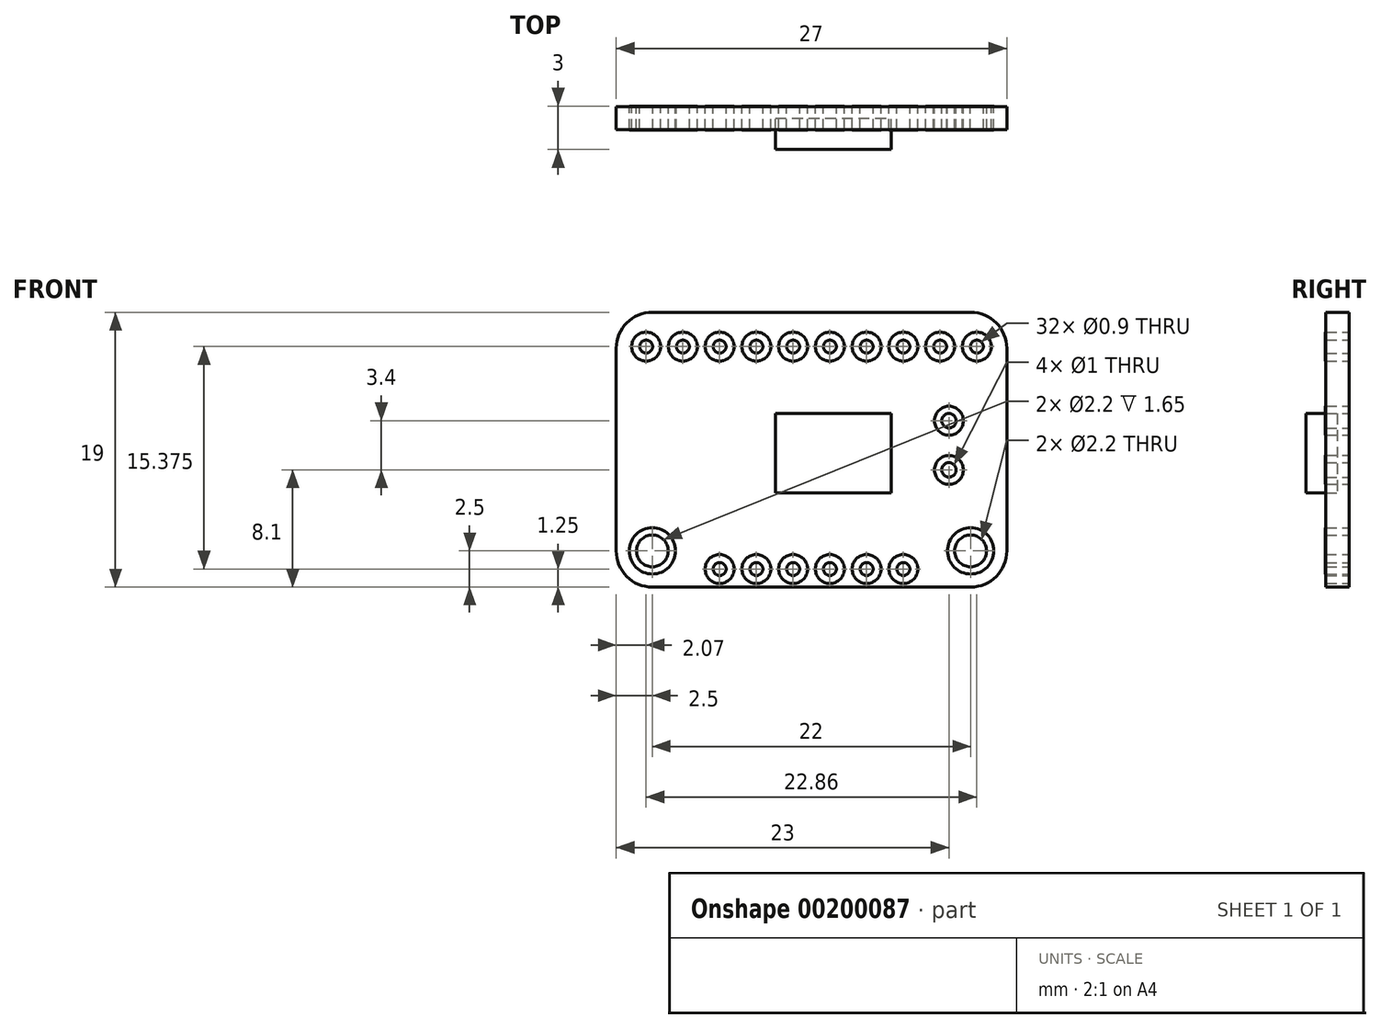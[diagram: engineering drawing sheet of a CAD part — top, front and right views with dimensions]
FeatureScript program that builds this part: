
annotation { "Feature Type Name" : "Feature", "Feature Type Description" : "" }
export const myFeature = defineFeature(function(context is Context, id is Id, definition is map)
    precondition{}
    {
        {
            var Q0;
            Q0=qCreatedBy(makeId("Front.planeOp"),FACE);
            var sketch = newSketch(context, id + "F0", { "sketchPlane" : qUnion([Q0])});
            skLineSegment(sketch, "E0.bottom", {"start": v(11, 9.5) * mm, "end": v(-11, 9.5) * mm});
            skLineSegment(sketch, "E0.top", {"start": v(11, -9.5) * mm, "end": v(-11, -9.5) * mm});
            skLineSegment(sketch, "E0.left", {"start": v(13.5, 7) * mm, "end": v(13.5, -7) * mm});
            skLineSegment(sketch, "E0.right", {"start": v(-13.5, 7) * mm, "end": v(-13.5, -7) * mm});
            skPoint(sketch, "E0.middle", {"position": v(0, 0) * mm});
            skPoint(sketch, "E1.visualSharp", {"position": v(-13.5, 9.5) * mm});
            skArc(sketch, "E1.filletArc", {"start": v(-11, 9.5) * mm, "mid": v(-12.77, 8.77) * mm, "end": v(-13.5, 7) * mm});
            skPoint(sketch, "E2.visualSharp", {"position": v(13.5, 9.5) * mm});
            skArc(sketch, "E2.filletArc", {"start": v(13.5, 7) * mm, "mid": v(12.77, 8.77) * mm, "end": v(11, 9.5) * mm});
            skPoint(sketch, "E3.visualSharp", {"position": v(13.5, -9.5) * mm});
            skArc(sketch, "E3.filletArc", {"start": v(11, -9.5) * mm, "mid": v(12.77, -8.77) * mm, "end": v(13.5, -7) * mm});
            skPoint(sketch, "E4.visualSharp", {"position": v(-13.5, -9.5) * mm});
            skArc(sketch, "E4.filletArc", {"start": v(-13.5, -7) * mm, "mid": v(-12.77, -8.77) * mm, "end": v(-11, -9.5) * mm});
            skCircle(sketch, "E5", {"center": v(-11, -7) * mm, "radius": 1.1 * mm});
            skCircle(sketch, "E6", {"center": v(11, -7) * mm, "radius": 1.1 * mm});
            skLineSegment(sketch, "E7.bottom", {"start": v(-2.5, 2.5) * mm, "end": v(5.5, 2.5) * mm});
            skLineSegment(sketch, "E7.top", {"start": v(-2.5, -3) * mm, "end": v(5.5, -3) * mm});
            skLineSegment(sketch, "E7.left", {"start": v(-2.5, 2.5) * mm, "end": v(-2.5, -3) * mm});
            skLineSegment(sketch, "E7.right", {"start": v(5.5, 2.5) * mm, "end": v(5.5, -3) * mm});
            skPoint(sketch, "E7.middle", {"position": v(1.5, -0.25) * mm});
            skCircle(sketch, "E8", {"center": v(9.5, 2) * mm, "radius": 0.5 * mm});
            skCircle(sketch, "E9", {"center": v(9.5, -1.4) * mm, "radius": 0.5 * mm});
            skCircle(sketch, "E10", {"center": v(-11.43, 7.13) * mm, "radius": 0.45 * mm});
            skCircle(sketch, "E11.1.0.0", {"center": v(-8.9, 7.13) * mm, "radius": 0.45 * mm});
            skCircle(sketch, "E11.2.0.0", {"center": v(-6.35, 7.13) * mm, "radius": 0.45 * mm});
            skCircle(sketch, "E11.3.0.0", {"center": v(-3.81, 7.13) * mm, "radius": 0.45 * mm});
            skCircle(sketch, "E11.4.0.0", {"center": v(-1.27, 7.13) * mm, "radius": 0.45 * mm});
            skCircle(sketch, "E11.5.0.0", {"center": v(1.27, 7.13) * mm, "radius": 0.45 * mm});
            skCircle(sketch, "E11.6.0.0", {"center": v(3.8, 7.13) * mm, "radius": 0.45 * mm});
            skCircle(sketch, "E11.7.0.0", {"center": v(6.35, 7.13) * mm, "radius": 0.45 * mm});
            skCircle(sketch, "E11.8.0.0", {"center": v(8.89, 7.13) * mm, "radius": 0.45 * mm});
            skCircle(sketch, "E11.9.0.0", {"center": v(11.43, 7.13) * mm, "radius": 0.45 * mm});
            skLineSegment(sketch, "E11.direction1", {"start": v(-11.43, 7.13) * mm, "end": v(-8.89, 7.13) * mm, "construction": true});
            skCircle(sketch, "E12", {"center": v(-6.35, -8.25) * mm, "radius": 0.45 * mm});
            skCircle(sketch, "E13.1.0.0", {"center": v(-3.81, -8.25) * mm, "radius": 0.45 * mm});
            skCircle(sketch, "E13.2.0.0", {"center": v(-1.27, -8.25) * mm, "radius": 0.45 * mm});
            skCircle(sketch, "E13.3.0.0", {"center": v(1.27, -8.25) * mm, "radius": 0.45 * mm});
            skCircle(sketch, "E13.4.0.0", {"center": v(3.81, -8.25) * mm, "radius": 0.45 * mm});
            skCircle(sketch, "E13.5.0.0", {"center": v(6.35, -8.25) * mm, "radius": 0.45 * mm});
            skLineSegment(sketch, "E13.direction1", {"start": v(-6.35, -8.25) * mm, "end": v(-3.81, -8.25) * mm, "construction": true});
            skCircle(sketch, "E14", {"center": v(9.5, -1.4) * mm, "radius": 1 * mm});
            skCircle(sketch, "E15", {"center": v(9.5, 2) * mm, "radius": 1 * mm});
            skCircle(sketch, "E16", {"center": v(-6.35, -8.25) * mm, "radius": 1 * mm});
            skCircle(sketch, "E17.1.0.0", {"center": v(-3.81, -8.25) * mm, "radius": 1 * mm});
            skCircle(sketch, "E17.2.0.0", {"center": v(-1.27, -8.25) * mm, "radius": 1 * mm});
            skCircle(sketch, "E17.3.0.0", {"center": v(1.27, -8.25) * mm, "radius": 1 * mm});
            skCircle(sketch, "E17.4.0.0", {"center": v(3.8, -8.25) * mm, "radius": 1 * mm});
            skCircle(sketch, "E17.5.0.0", {"center": v(6.35, -8.25) * mm, "radius": 1 * mm});
            skCircle(sketch, "E18", {"center": v(-11.43, 7.13) * mm, "radius": 1 * mm});
            skCircle(sketch, "E19.1.0.0", {"center": v(-8.9, 7.13) * mm, "radius": 1 * mm});
            skCircle(sketch, "E19.2.0.0", {"center": v(-6.35, 7.13) * mm, "radius": 1 * mm});
            skCircle(sketch, "E19.3.0.0", {"center": v(-3.81, 7.13) * mm, "radius": 1 * mm});
            skCircle(sketch, "E19.4.0.0", {"center": v(-1.27, 7.13) * mm, "radius": 1 * mm});
            skCircle(sketch, "E19.5.0.0", {"center": v(1.27, 7.13) * mm, "radius": 1 * mm});
            skCircle(sketch, "E19.6.0.0", {"center": v(3.8, 7.13) * mm, "radius": 1 * mm});
            skCircle(sketch, "E19.7.0.0", {"center": v(6.35, 7.13) * mm, "radius": 1 * mm});
            skCircle(sketch, "E19.8.0.0", {"center": v(8.89, 7.13) * mm, "radius": 1 * mm});
            skCircle(sketch, "E19.9.0.0", {"center": v(11.43, 7.13) * mm, "radius": 1 * mm});
            skLineSegment(sketch, "E19.direction1", {"start": v(-11.43, 7.13) * mm, "end": v(-8.9, 7.13) * mm, "construction": true});
            skCircle(sketch, "E20", {"center": v(-11, -7) * mm, "radius": 1.6 * mm});
            skCircle(sketch, "E21", {"center": v(11, -7) * mm, "radius": 1.6 * mm});
            skSolve(sketch);
        }
        {
            var Q0;
            Q0=makeQuery(id+"F0.imprint","IMPRINT",FACE,{"disambiguationData":[TD([[makeQuery(id+"F0.imprint","IMPRINT",EDGE,{"derivedFrom":sQuery(id+"F0.wireOp",EDGE,"E0.bottom")}),1.0]])]});
            var Q1;
            Q1=makeQuery(id+"F0.imprint","IMPRINT",FACE,{"disambiguationData":[TD([[makeQuery(id+"F0.imprint","IMPRINT",EDGE,{"derivedFrom":sQuery(id+"F0.wireOp",EDGE,"E7.bottom")}),-1.0]])]});
            var Q2;
            Q2=makeQuery(id+"F0.imprint","IMPRINT",FACE,{"disambiguationData":[TD([[makeQuery(id+"F0.imprint","IMPRINT",EDGE,{"derivedFrom":sQuery(id+"F0.wireOp",EDGE,"E10")}),-1.0]])]});
            var Q3;
            Q3=makeQuery(id+"F0.imprint","IMPRINT",FACE,{"disambiguationData":[TD([[makeQuery(id+"F0.imprint","IMPRINT",EDGE,{"derivedFrom":sQuery(id+"F0.wireOp",EDGE,"E11.1.0.0")}),-1.0]])]});
            var Q4;
            Q4=makeQuery(id+"F0.imprint","IMPRINT",FACE,{"disambiguationData":[TD([[makeQuery(id+"F0.imprint","IMPRINT",EDGE,{"derivedFrom":sQuery(id+"F0.wireOp",EDGE,"E11.2.0.0")}),-1.0]])]});
            var Q5;
            Q5=makeQuery(id+"F0.imprint","IMPRINT",FACE,{"disambiguationData":[TD([[makeQuery(id+"F0.imprint","IMPRINT",EDGE,{"derivedFrom":sQuery(id+"F0.wireOp",EDGE,"E11.3.0.0")}),-1.0]])]});
            var Q6;
            Q6=makeQuery(id+"F0.imprint","IMPRINT",FACE,{"disambiguationData":[TD([[makeQuery(id+"F0.imprint","IMPRINT",EDGE,{"derivedFrom":sQuery(id+"F0.wireOp",EDGE,"E11.4.0.0")}),-1.0]])]});
            var Q7;
            Q7=makeQuery(id+"F0.imprint","IMPRINT",FACE,{"disambiguationData":[TD([[makeQuery(id+"F0.imprint","IMPRINT",EDGE,{"derivedFrom":sQuery(id+"F0.wireOp",EDGE,"E11.5.0.0")}),-1.0]])]});
            var Q8;
            Q8=makeQuery(id+"F0.imprint","IMPRINT",FACE,{"disambiguationData":[TD([[makeQuery(id+"F0.imprint","IMPRINT",EDGE,{"derivedFrom":sQuery(id+"F0.wireOp",EDGE,"E11.6.0.0")}),-1.0]])]});
            var Q9;
            Q9=makeQuery(id+"F0.imprint","IMPRINT",FACE,{"disambiguationData":[TD([[makeQuery(id+"F0.imprint","IMPRINT",EDGE,{"derivedFrom":sQuery(id+"F0.wireOp",EDGE,"E11.7.0.0")}),-1.0]])]});
            var Q10;
            Q10=makeQuery(id+"F0.imprint","IMPRINT",FACE,{"disambiguationData":[TD([[makeQuery(id+"F0.imprint","IMPRINT",EDGE,{"derivedFrom":sQuery(id+"F0.wireOp",EDGE,"E11.8.0.0")}),-1.0]])]});
            var Q11;
            Q11=makeQuery(id+"F0.imprint","IMPRINT",FACE,{"disambiguationData":[TD([[makeQuery(id+"F0.imprint","IMPRINT",EDGE,{"derivedFrom":sQuery(id+"F0.wireOp",EDGE,"E11.9.0.0")}),-1.0]])]});
            var Q12;
            Q12=makeQuery(id+"F0.imprint","IMPRINT",FACE,{"disambiguationData":[TD([[makeQuery(id+"F0.imprint","IMPRINT",EDGE,{"derivedFrom":sQuery(id+"F0.wireOp",EDGE,"E8")}),-1.0]])]});
            var Q13;
            Q13=makeQuery(id+"F0.imprint","IMPRINT",FACE,{"disambiguationData":[TD([[makeQuery(id+"F0.imprint","IMPRINT",EDGE,{"derivedFrom":sQuery(id+"F0.wireOp",EDGE,"E9")}),-1.0]])]});
            var Q14;
            Q14=makeQuery(id+"F0.imprint","IMPRINT",FACE,{"disambiguationData":[TD([[makeQuery(id+"F0.imprint","IMPRINT",EDGE,{"derivedFrom":sQuery(id+"F0.wireOp",EDGE,"E13.5.0.0")}),-1.0]])]});
            var Q15;
            Q15=makeQuery(id+"F0.imprint","IMPRINT",FACE,{"disambiguationData":[TD([[makeQuery(id+"F0.imprint","IMPRINT",EDGE,{"derivedFrom":sQuery(id+"F0.wireOp",EDGE,"E13.4.0.0")}),-1.0]])]});
            var Q16;
            Q16=makeQuery(id+"F0.imprint","IMPRINT",FACE,{"disambiguationData":[TD([[makeQuery(id+"F0.imprint","IMPRINT",EDGE,{"derivedFrom":sQuery(id+"F0.wireOp",EDGE,"E13.3.0.0")}),-1.0]])]});
            var Q17;
            Q17=makeQuery(id+"F0.imprint","IMPRINT",FACE,{"disambiguationData":[TD([[makeQuery(id+"F0.imprint","IMPRINT",EDGE,{"derivedFrom":sQuery(id+"F0.wireOp",EDGE,"E13.2.0.0")}),-1.0]])]});
            var Q18;
            Q18=makeQuery(id+"F0.imprint","IMPRINT",FACE,{"disambiguationData":[TD([[makeQuery(id+"F0.imprint","IMPRINT",EDGE,{"derivedFrom":sQuery(id+"F0.wireOp",EDGE,"E13.1.0.0")}),-1.0]])]});
            var Q19;
            Q19=makeQuery(id+"F0.imprint","IMPRINT",FACE,{"disambiguationData":[TD([[makeQuery(id+"F0.imprint","IMPRINT",EDGE,{"derivedFrom":sQuery(id+"F0.wireOp",EDGE,"E12")}),-1.0]])]});
            var Q20;
            Q20=makeQuery(id+"F0.imprint","IMPRINT",FACE,{"disambiguationData":[TD([[makeQuery(id+"F0.imprint","IMPRINT",EDGE,{"derivedFrom":sQuery(id+"F0.wireOp",EDGE,"E6")}),-1.0]])]});
            var Q21;
            Q21=makeQuery(id+"F0.imprint","IMPRINT",FACE,{"disambiguationData":[TD([[makeQuery(id+"F0.imprint","IMPRINT",EDGE,{"derivedFrom":sQuery(id+"F0.wireOp",EDGE,"E5")}),-1.0]])]});
            extrude(context, id + "F1", {"entities" : qUnion([Q0, Q1, Q2, Q3, Q4, Q5, Q6, Q7, Q8, Q9, Q10, Q11, Q12, Q13, Q14, Q15, Q16, Q17, Q18, Q19, Q20, Q21]), "endBound" : BoundingType.SYMMETRIC, "depth" : 1.6 * mm});
        }
        {
            var Q0;
            Q0=makeQuery(id+"F0.imprint","IMPRINT",FACE,{"disambiguationData":[TD([[makeQuery(id+"F0.imprint","IMPRINT",EDGE,{"derivedFrom":sQuery(id+"F0.wireOp",EDGE,"E5")}),-1.0]])]});
            var Q1;
            Q1=makeQuery(id+"F0.imprint","IMPRINT",FACE,{"disambiguationData":[TD([[makeQuery(id+"F0.imprint","IMPRINT",EDGE,{"derivedFrom":sQuery(id+"F0.wireOp",EDGE,"E12")}),-1.0]])]});
            var Q2;
            Q2=makeQuery(id+"F0.imprint","IMPRINT",FACE,{"disambiguationData":[TD([[makeQuery(id+"F0.imprint","IMPRINT",EDGE,{"derivedFrom":sQuery(id+"F0.wireOp",EDGE,"E13.2.0.0")}),-1.0]])]});
            var Q3;
            Q3=makeQuery(id+"F0.imprint","IMPRINT",FACE,{"disambiguationData":[TD([[makeQuery(id+"F0.imprint","IMPRINT",EDGE,{"derivedFrom":sQuery(id+"F0.wireOp",EDGE,"E13.1.0.0")}),-1.0]])]});
            var Q4;
            Q4=makeQuery(id+"F0.imprint","IMPRINT",FACE,{"disambiguationData":[TD([[makeQuery(id+"F0.imprint","IMPRINT",EDGE,{"derivedFrom":sQuery(id+"F0.wireOp",EDGE,"E13.3.0.0")}),-1.0]])]});
            var Q5;
            Q5=makeQuery(id+"F0.imprint","IMPRINT",FACE,{"disambiguationData":[TD([[makeQuery(id+"F0.imprint","IMPRINT",EDGE,{"derivedFrom":sQuery(id+"F0.wireOp",EDGE,"E13.4.0.0")}),-1.0]])]});
            var Q6;
            Q6=makeQuery(id+"F0.imprint","IMPRINT",FACE,{"disambiguationData":[TD([[makeQuery(id+"F0.imprint","IMPRINT",EDGE,{"derivedFrom":sQuery(id+"F0.wireOp",EDGE,"E13.5.0.0")}),-1.0]])]});
            var Q7;
            Q7=makeQuery(id+"F0.imprint","IMPRINT",FACE,{"disambiguationData":[TD([[makeQuery(id+"F0.imprint","IMPRINT",EDGE,{"derivedFrom":sQuery(id+"F0.wireOp",EDGE,"E6")}),-1.0]])]});
            var Q8;
            Q8=makeQuery(id+"F0.imprint","IMPRINT",FACE,{"disambiguationData":[TD([[makeQuery(id+"F0.imprint","IMPRINT",EDGE,{"derivedFrom":sQuery(id+"F0.wireOp",EDGE,"E9")}),-1.0]])]});
            var Q9;
            Q9=makeQuery(id+"F0.imprint","IMPRINT",FACE,{"disambiguationData":[TD([[makeQuery(id+"F0.imprint","IMPRINT",EDGE,{"derivedFrom":sQuery(id+"F0.wireOp",EDGE,"E8")}),-1.0]])]});
            var Q10;
            Q10=makeQuery(id+"F0.imprint","IMPRINT",FACE,{"disambiguationData":[TD([[makeQuery(id+"F0.imprint","IMPRINT",EDGE,{"derivedFrom":sQuery(id+"F0.wireOp",EDGE,"E11.9.0.0")}),-1.0]])]});
            var Q11;
            Q11=makeQuery(id+"F0.imprint","IMPRINT",FACE,{"disambiguationData":[TD([[makeQuery(id+"F0.imprint","IMPRINT",EDGE,{"derivedFrom":sQuery(id+"F0.wireOp",EDGE,"E11.8.0.0")}),-1.0]])]});
            var Q12;
            Q12=makeQuery(id+"F0.imprint","IMPRINT",FACE,{"disambiguationData":[TD([[makeQuery(id+"F0.imprint","IMPRINT",EDGE,{"derivedFrom":sQuery(id+"F0.wireOp",EDGE,"E11.7.0.0")}),-1.0]])]});
            var Q13;
            Q13=makeQuery(id+"F0.imprint","IMPRINT",FACE,{"disambiguationData":[TD([[makeQuery(id+"F0.imprint","IMPRINT",EDGE,{"derivedFrom":sQuery(id+"F0.wireOp",EDGE,"E11.6.0.0")}),-1.0]])]});
            var Q14;
            Q14=makeQuery(id+"F0.imprint","IMPRINT",FACE,{"disambiguationData":[TD([[makeQuery(id+"F0.imprint","IMPRINT",EDGE,{"derivedFrom":sQuery(id+"F0.wireOp",EDGE,"E11.5.0.0")}),-1.0]])]});
            var Q15;
            Q15=makeQuery(id+"F0.imprint","IMPRINT",FACE,{"disambiguationData":[TD([[makeQuery(id+"F0.imprint","IMPRINT",EDGE,{"derivedFrom":sQuery(id+"F0.wireOp",EDGE,"E11.4.0.0")}),-1.0]])]});
            var Q16;
            Q16=makeQuery(id+"F0.imprint","IMPRINT",FACE,{"disambiguationData":[TD([[makeQuery(id+"F0.imprint","IMPRINT",EDGE,{"derivedFrom":sQuery(id+"F0.wireOp",EDGE,"E11.3.0.0")}),-1.0]])]});
            var Q17;
            Q17=makeQuery(id+"F0.imprint","IMPRINT",FACE,{"disambiguationData":[TD([[makeQuery(id+"F0.imprint","IMPRINT",EDGE,{"derivedFrom":sQuery(id+"F0.wireOp",EDGE,"E11.2.0.0")}),-1.0]])]});
            var Q18;
            Q18=makeQuery(id+"F0.imprint","IMPRINT",FACE,{"disambiguationData":[TD([[makeQuery(id+"F0.imprint","IMPRINT",EDGE,{"derivedFrom":sQuery(id+"F0.wireOp",EDGE,"E11.1.0.0")}),-1.0]])]});
            var Q19;
            Q19=makeQuery(id+"F0.imprint","IMPRINT",FACE,{"disambiguationData":[TD([[makeQuery(id+"F0.imprint","IMPRINT",EDGE,{"derivedFrom":sQuery(id+"F0.wireOp",EDGE,"E10")}),-1.0]])]});
            extrude(context, id + "F2", {"entities" : qUnion([Q0, Q1, Q2, Q3, Q4, Q5, Q6, Q7, Q8, Q9, Q10, Q11, Q12, Q13, Q14, Q15, Q16, Q17, Q18, Q19]), "endBound" : BoundingType.SYMMETRIC, "depth" : 1.65 * mm});
        }
        {
            var Q0;
            Q0=makeQuery(id+"F0.imprint","IMPRINT",FACE,{"disambiguationData":[TD([[makeQuery(id+"F0.imprint","IMPRINT",EDGE,{"derivedFrom":sQuery(id+"F0.wireOp",EDGE,"E7.bottom")}),-1.0]])]});
            extrude(context, id + "F3", {"entities" : qUnion([Q0]), "depth" : 2.17 * mm});
        }
    });
